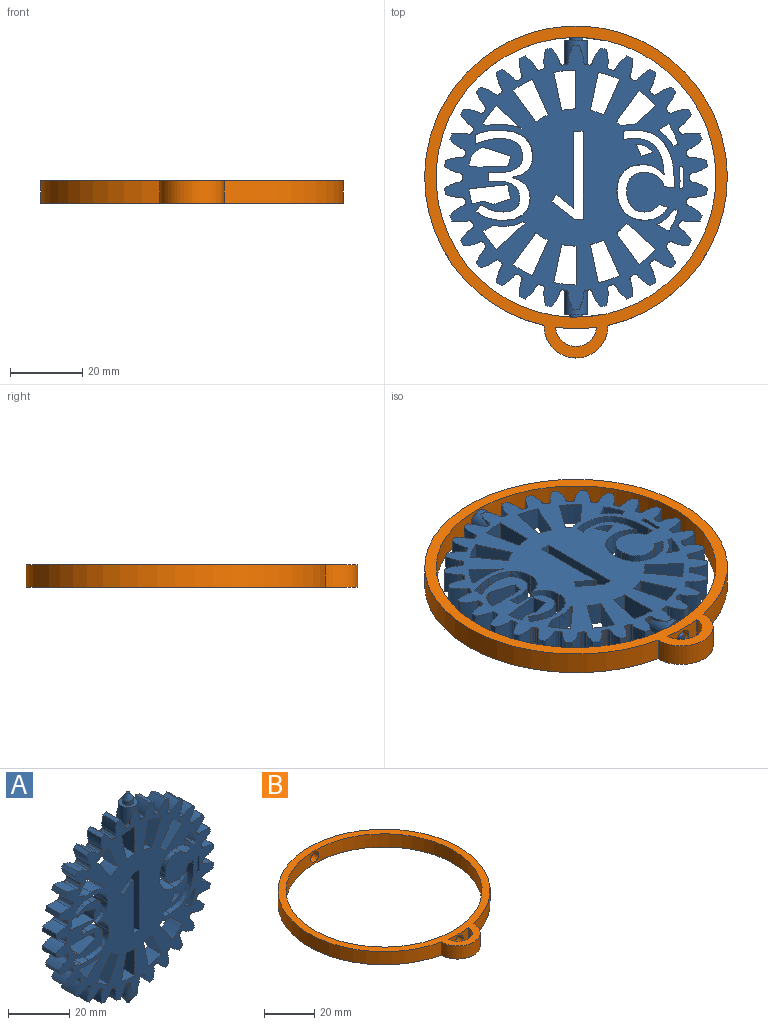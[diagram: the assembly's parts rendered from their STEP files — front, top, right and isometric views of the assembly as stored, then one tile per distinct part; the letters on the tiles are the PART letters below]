
ASSEMBLY  parts=2 mates=1
PART A: 350 faces, bbox 72.9x6.4x83.8 mm
  f0: cylinder r=36.58mm len=0.84mm, axis (0,1,0), area 0mm2, adj f24,f95,f341
  f1: cylinder r=36.58mm len=0.84mm, axis (0,1,0), area 0mm2, adj f24,f92,f341
  f2: cylinder r=36.58mm len=0.84mm, axis (0,1,0), area 0mm2, adj f3,f25,f341
  f3: extruded ~4.4x1.33mm, area 2.4mm2, adj f2,f4,f25,f341
  f4: cylinder r=0.84mm len=1.95mm, axis (0,1,0), area 1.8mm2, adj f3,f25,f91,f341
  f5: extruded ~4.4x1.33mm, area 2.4mm2, adj f6,f25,f47,f341
  f6: cylinder r=0.84mm len=1.95mm, axis (0,1,0), area 1.8mm2, adj f5,f25,f96,f341
  f7: cylinder r=36.58mm len=0.84mm, axis (0,1,0), area 0mm2, adj f12,f25,f336
  f8: cylinder r=36.58mm len=0.84mm, axis (0,1,0), area 0mm2, adj f18,f25,f336
  f9: cylinder r=36.58mm len=0.84mm, axis (0,1,0), area 0mm2, adj f17,f24,f336
  f10: cylinder r=36.58mm len=0.84mm, axis (0,1,0), area 0mm2, adj f11,f24,f336
  f11: extruded ~4.4x1.33mm, area 2.4mm2, adj f10,f14,f24,f336
  f12: extruded ~4.4x1.33mm, area 2.4mm2, adj f7,f15,f25,f336
  f13: cylinder r=31.43mm len=6.35mm, axis (0,1,0), area 4.6mm2, adj f14,f15,f24,f25,f196,f336
  f14: cylinder r=0.84mm len=1.95mm, axis (0,1,0), area 1.8mm2, adj f11,f13,f24,f336
  f15: cylinder r=0.84mm len=1.95mm, axis (0,1,0), area 1.8mm2, adj f12,f13,f25,f336
  f16: cylinder r=31.43mm len=6.35mm, axis (0,1,0), area 4.6mm2, adj f19,f20,f24,f25,f198,f336
  f17: extruded ~4.4x1.33mm, area 2.4mm2, adj f9,f19,f24,f336
  f18: extruded ~4.4x1.33mm, area 2.4mm2, adj f8,f20,f25,f336
  f19: cylinder r=0.84mm len=1.95mm, axis (0,1,0), area 1.8mm2, adj f16,f17,f24,f336
  f20: cylinder r=0.84mm len=1.95mm, axis (0,1,0), area 1.8mm2, adj f16,f18,f25,f336
  f21: plane 6.35x2.78mm, normal (0.1,0,-0.99), area 17.8mm2, adj f23,f24,f25,f333
  f22: plane 6.35x2.47mm, normal (-0.31,0,0.95), area 16.5mm2, adj f24,f25,f200,f327
  f23: extruded ~6.35x1.68mm, area 10.7mm2, adj f21,f24,f25,f199
  f24: plane 73.15x72.91mm, normal (0,-1,0), area 2651.2mm2, adj f0,f1,f9,f10,f11,f13,f14,f16
  f25: plane 73.15x72.91mm, normal (0,1,0), area 2651.2mm2, adj f2,f3,f4,f5,f6,f7,f8,f12
  f26: cylinder r=36.58mm len=6.35mm, axis (0,1,0), area 10.7mm2, adj f24,f25,f190,f195
  f27: cylinder r=36.58mm len=6.35mm, axis (0,1,0), area 10.7mm2, adj f24,f25,f185,f192
  f28: cylinder r=36.58mm len=6.35mm, axis (0,1,0), area 10.7mm2, adj f24,f25,f175,f187
  f29: cylinder r=36.58mm len=6.35mm, axis (0,1,0), area 10.7mm2, adj f24,f25,f170,f182
  f30: cylinder r=36.58mm len=6.35mm, axis (0,1,0), area 10.7mm2, adj f24,f25,f177,f180
  f31: cylinder r=36.58mm len=6.35mm, axis (0,1,0), area 10.7mm2, adj f24,f25,f165,f172
  f32: cylinder r=36.58mm len=6.35mm, axis (0,1,0), area 10.7mm2, adj f24,f25,f55,f167
  f33: cylinder r=36.58mm len=6.35mm, axis (0,1,0), area 10.7mm2, adj f24,f25,f150,f162
  f34: cylinder r=36.58mm len=6.35mm, axis (0,1,0), area 10.7mm2, adj f24,f25,f157,f160
  f35: cylinder r=36.58mm len=6.35mm, axis (0,1,0), area 10.7mm2, adj f24,f25,f145,f152
  f36: cylinder r=36.58mm len=6.35mm, axis (0,1,0), area 10.7mm2, adj f24,f25,f147,f197
  f37: cylinder r=36.58mm len=6.35mm, axis (0,1,0), area 10.7mm2, adj f24,f25,f142,f155
  f38: cylinder r=36.58mm len=6.35mm, axis (0,1,0), area 10.7mm2, adj f24,f25,f137,f140
  f39: cylinder r=36.58mm len=6.35mm, axis (0,1,0), area 10.7mm2, adj f24,f25,f132,f135
  f40: cylinder r=36.58mm len=6.35mm, axis (0,1,0), area 10.7mm2, adj f24,f25,f127,f130
  f41: cylinder r=36.58mm len=6.35mm, axis (0,1,0), area 10.7mm2, adj f24,f25,f110,f122
  f42: cylinder r=36.58mm len=6.35mm, axis (0,1,0), area 10.7mm2, adj f24,f25,f117,f120
  f43: cylinder r=36.58mm len=6.35mm, axis (0,1,0), area 10.7mm2, adj f24,f25,f105,f112
  f44: cylinder r=36.58mm len=6.35mm, axis (0,1,0), area 10.7mm2, adj f24,f25,f107,f125
  f45: cylinder r=36.58mm len=6.35mm, axis (0,1,0), area 10.7mm2, adj f24,f25,f102,f115
  f46: cylinder r=36.58mm len=6.35mm, axis (0,1,0), area 10.7mm2, adj f24,f25,f97,f100
  f47: cylinder r=36.58mm len=0.84mm, axis (0,1,0), area 0mm2, adj f5,f25,f341
  f48: cylinder r=36.58mm len=6.35mm, axis (0,1,0), area 10.7mm2, adj f24,f25,f87,f90
  f49: cylinder r=36.58mm len=6.35mm, axis (0,1,0), area 10.7mm2, adj f24,f25,f75,f82
  f50: cylinder r=36.58mm len=6.35mm, axis (0,1,0), area 10.7mm2, adj f24,f25,f65,f77
  f51: cylinder r=36.58mm len=6.35mm, axis (0,1,0), area 10.7mm2, adj f24,f25,f72,f85
  f52: cylinder r=36.58mm len=6.35mm, axis (0,1,0), area 10.7mm2, adj f24,f25,f67,f70
  f53: cylinder r=36.58mm len=6.35mm, axis (0,1,0), area 10.7mm2, adj f24,f25,f62,f80
  f54: cylinder r=36.58mm len=6.35mm, axis (0,1,0), area 10.7mm2, adj f24,f25,f57,f60
  f55: extruded ~6.35x4.24mm, area 29.4mm2, adj f24,f25,f32,f58
  f56: cylinder r=31.43mm len=6.35mm, axis (0,1,0), area 4.6mm2, adj f24,f25,f58,f59
  f57: extruded ~6.35x4.24mm, area 29.4mm2, adj f24,f25,f54,f59
  f58: cylinder r=0.84mm len=6.35mm, axis (0,1,0), area 8.1mm2, adj f24,f25,f55,f56
  f59: cylinder r=0.84mm len=6.35mm, axis (0,1,0), area 8.1mm2, adj f24,f25,f56,f57
  f60: extruded ~6.35x4.51mm, area 29.4mm2, adj f24,f25,f54,f63
  f61: cylinder r=31.43mm len=6.35mm, axis (0,1,0), area 4.6mm2, adj f24,f25,f63,f64
  f62: extruded ~6.35x3.77mm, area 29.4mm2, adj f24,f25,f53,f64
  f63: cylinder r=0.84mm len=6.35mm, axis (0,1,0), area 8.1mm2, adj f24,f25,f60,f61
  f64: cylinder r=0.84mm len=6.35mm, axis (0,1,0), area 8.1mm2, adj f24,f25,f61,f62
  f65: extruded ~6.35x4.16mm, area 29.4mm2, adj f24,f25,f50,f68
  f66: cylinder r=31.43mm len=6.35mm, axis (0,1,0), area 4.6mm2, adj f24,f25,f68,f69
  f67: extruded ~6.35x4.34mm, area 29.4mm2, adj f24,f25,f52,f69
  f68: cylinder r=0.84mm len=6.35mm, axis (0,1,0), area 8.1mm2, adj f24,f25,f65,f66
  f69: cylinder r=0.84mm len=6.35mm, axis (0,1,0), area 8.1mm2, adj f24,f25,f66,f67
  f70: extruded ~6.35x3.66mm, area 29.4mm2, adj f24,f25,f52,f73
  f71: cylinder r=31.43mm len=6.35mm, axis (0,1,0), area 4.6mm2, adj f24,f25,f73,f74
  f72: extruded ~6.35x4.56mm, area 29.4mm2, adj f24,f25,f51,f74
  f73: cylinder r=0.84mm len=6.35mm, axis (0,1,0), area 8.1mm2, adj f24,f25,f70,f71
  f74: cylinder r=0.84mm len=6.35mm, axis (0,1,0), area 8.1mm2, adj f24,f25,f71,f72
  f75: extruded ~6.35x4.47mm, area 29.4mm2, adj f24,f25,f49,f78
  f76: cylinder r=31.43mm len=6.35mm, axis (0,1,0), area 4.6mm2, adj f24,f25,f78,f79
  f77: extruded ~6.35x3.93mm, area 29.4mm2, adj f24,f25,f50,f79
  f78: cylinder r=0.84mm len=6.35mm, axis (0,1,0), area 8.1mm2, adj f24,f25,f75,f76
  f79: cylinder r=0.84mm len=6.35mm, axis (0,1,0), area 8.1mm2, adj f24,f25,f76,f77
  f80: extruded ~6.35x4.59mm, area 29.4mm2, adj f24,f25,f53,f83
  f81: cylinder r=31.43mm len=6.35mm, axis (0,1,0), area 4.6mm2, adj f24,f25,f83,f84
  f82: extruded ~6.35x3.35mm, area 29.4mm2, adj f24,f25,f49,f84
  f83: cylinder r=0.84mm len=6.35mm, axis (0,1,0), area 8.1mm2, adj f24,f25,f80,f81
  f84: cylinder r=0.84mm len=6.35mm, axis (0,1,0), area 8.1mm2, adj f24,f25,f81,f82
  f85: extruded ~6.35x3.48mm, area 29.4mm2, adj f24,f25,f51,f88
  f86: cylinder r=31.43mm len=6.35mm, axis (0,1,0), area 4.6mm2, adj f24,f25,f88,f89
  f87: extruded ~6.35x4.58mm, area 29.4mm2, adj f24,f25,f48,f89
  f88: cylinder r=0.84mm len=6.35mm, axis (0,1,0), area 8.1mm2, adj f24,f25,f85,f86
  f89: cylinder r=0.84mm len=6.35mm, axis (0,1,0), area 8.1mm2, adj f24,f25,f86,f87
  f90: extruded ~6.35x4.03mm, area 29.4mm2, adj f24,f25,f48,f93
  f91: cylinder r=31.43mm len=6.35mm, axis (0,1,0), area 4.3mm2, adj f4,f24,f25,f93,f94,f341
  f92: extruded ~4.4x1.33mm, area 2.4mm2, adj f1,f24,f94,f341
  f93: cylinder r=0.84mm len=6.35mm, axis (0,1,0), area 8.1mm2, adj f24,f25,f90,f91
  f94: cylinder r=0.84mm len=1.95mm, axis (0,1,0), area 1.8mm2, adj f24,f91,f92,f341
  f95: extruded ~4.4x1.33mm, area 2.4mm2, adj f0,f24,f98,f341
  f96: cylinder r=31.43mm len=6.35mm, axis (0,1,0), area 4.6mm2, adj f6,f24,f25,f98,f99,f341
  f97: extruded ~6.35x4.03mm, area 29.4mm2, adj f24,f25,f46,f99
  f98: cylinder r=0.84mm len=1.95mm, axis (0,1,0), area 1.8mm2, adj f24,f95,f96,f341
  f99: cylinder r=0.84mm len=6.35mm, axis (0,1,0), area 8.1mm2, adj f24,f25,f96,f97
  f100: extruded ~6.35x4.58mm, area 29.4mm2, adj f24,f25,f46,f103
  f101: cylinder r=31.43mm len=6.35mm, axis (0,1,0), area 4.6mm2, adj f24,f25,f103,f104
  f102: extruded ~6.35x3.48mm, area 29.4mm2, adj f24,f25,f45,f104
  f103: cylinder r=0.84mm len=6.35mm, axis (0,1,0), area 8.1mm2, adj f24,f25,f100,f101
  f104: cylinder r=0.84mm len=6.35mm, axis (0,1,0), area 8.1mm2, adj f24,f25,f101,f102
  f105: extruded ~6.35x3.35mm, area 29.4mm2, adj f24,f25,f43,f108
  f106: cylinder r=31.43mm len=6.35mm, axis (0,1,0), area 4.6mm2, adj f24,f25,f108,f109
  f107: extruded ~6.35x4.59mm, area 29.4mm2, adj f24,f25,f44,f109
  f108: cylinder r=0.84mm len=6.35mm, axis (0,1,0), area 8.1mm2, adj f24,f25,f105,f106
  f109: cylinder r=0.84mm len=6.35mm, axis (0,1,0), area 8.1mm2, adj f24,f25,f106,f107
  f110: extruded ~6.35x3.93mm, area 29.4mm2, adj f24,f25,f41,f113
  f111: cylinder r=31.43mm len=6.35mm, axis (0,1,0), area 4.6mm2, adj f24,f25,f113,f114
  f112: extruded ~6.35x4.47mm, area 29.4mm2, adj f24,f25,f43,f114
  f113: cylinder r=0.84mm len=6.35mm, axis (0,1,0), area 8.1mm2, adj f24,f25,f110,f111
  f114: cylinder r=0.84mm len=6.35mm, axis (0,1,0), area 8.1mm2, adj f24,f25,f111,f112
  f115: extruded ~6.35x4.56mm, area 29.4mm2, adj f24,f25,f45,f118
  f116: cylinder r=31.43mm len=6.35mm, axis (0,1,0), area 4.6mm2, adj f24,f25,f118,f119
  f117: extruded ~6.35x3.66mm, area 29.4mm2, adj f24,f25,f42,f119
  f118: cylinder r=0.84mm len=6.35mm, axis (0,1,0), area 8.1mm2, adj f24,f25,f115,f116
  f119: cylinder r=0.84mm len=6.35mm, axis (0,1,0), area 8.1mm2, adj f24,f25,f116,f117
  f120: extruded ~6.35x4.34mm, area 29.4mm2, adj f24,f25,f42,f123
  f121: cylinder r=31.43mm len=6.35mm, axis (0,1,0), area 4.6mm2, adj f24,f25,f123,f124
  f122: extruded ~6.35x4.16mm, area 29.4mm2, adj f24,f25,f41,f124
  f123: cylinder r=0.84mm len=6.35mm, axis (0,1,0), area 8.1mm2, adj f24,f25,f120,f121
  f124: cylinder r=0.84mm len=6.35mm, axis (0,1,0), area 8.1mm2, adj f24,f25,f121,f122
  f125: extruded ~6.35x3.77mm, area 29.4mm2, adj f24,f25,f44,f128
  f126: cylinder r=31.43mm len=6.35mm, axis (0,1,0), area 4.6mm2, adj f24,f25,f128,f129
  f127: extruded ~6.35x4.51mm, area 29.4mm2, adj f24,f25,f40,f129
  f128: cylinder r=0.84mm len=6.35mm, axis (0,1,0), area 8.1mm2, adj f24,f25,f125,f126
  f129: cylinder r=0.84mm len=6.35mm, axis (0,1,0), area 8.1mm2, adj f24,f25,f126,f127
  f130: extruded ~6.35x4.24mm, area 29.4mm2, adj f24,f25,f40,f133
  f131: cylinder r=31.43mm len=6.35mm, axis (0,1,0), area 4.6mm2, adj f24,f25,f133,f134
  f132: extruded ~6.35x4.24mm, area 29.4mm2, adj f24,f25,f39,f134
  f133: cylinder r=0.84mm len=6.35mm, axis (0,1,0), area 8.1mm2, adj f24,f25,f130,f131
  f134: cylinder r=0.84mm len=6.35mm, axis (0,1,0), area 8.1mm2, adj f24,f25,f131,f132
  f135: extruded ~6.35x4.51mm, area 29.4mm2, adj f24,f25,f39,f138
  f136: cylinder r=31.43mm len=6.35mm, axis (0,1,0), area 4.6mm2, adj f24,f25,f138,f139
  f137: extruded ~6.35x3.77mm, area 29.4mm2, adj f24,f25,f38,f139
  f138: cylinder r=0.84mm len=6.35mm, axis (0,1,0), area 8.1mm2, adj f24,f25,f135,f136
  f139: cylinder r=0.84mm len=6.35mm, axis (0,1,0), area 8.1mm2, adj f24,f25,f136,f137
  f140: extruded ~6.35x4.59mm, area 29.4mm2, adj f24,f25,f38,f143
  f141: cylinder r=31.43mm len=6.35mm, axis (0,1,0), area 4.6mm2, adj f24,f25,f143,f144
  f142: extruded ~6.35x3.35mm, area 29.4mm2, adj f24,f25,f37,f144
  f143: cylinder r=0.84mm len=6.35mm, axis (0,1,0), area 8.1mm2, adj f24,f25,f140,f141
  f144: cylinder r=0.84mm len=6.35mm, axis (0,1,0), area 8.1mm2, adj f24,f25,f141,f142
  f145: extruded ~6.35x3.48mm, area 29.4mm2, adj f24,f25,f35,f148
  f146: cylinder r=31.43mm len=6.35mm, axis (0,1,0), area 4.6mm2, adj f24,f25,f148,f149
  f147: extruded ~6.35x4.58mm, area 29.4mm2, adj f24,f25,f36,f149
  f148: cylinder r=0.84mm len=6.35mm, axis (0,1,0), area 8.1mm2, adj f24,f25,f145,f146
  f149: cylinder r=0.84mm len=6.35mm, axis (0,1,0), area 8.1mm2, adj f24,f25,f146,f147
  f150: extruded ~6.35x3.66mm, area 29.4mm2, adj f24,f25,f33,f153
  f151: cylinder r=31.43mm len=6.35mm, axis (0,1,0), area 4.6mm2, adj f24,f25,f153,f154
  f152: extruded ~6.35x4.56mm, area 29.4mm2, adj f24,f25,f35,f154
  f153: cylinder r=0.84mm len=6.35mm, axis (0,1,0), area 8.1mm2, adj f24,f25,f150,f151
  f154: cylinder r=0.84mm len=6.35mm, axis (0,1,0), area 8.1mm2, adj f24,f25,f151,f152
  f155: extruded ~6.35x4.47mm, area 29.4mm2, adj f24,f25,f37,f158
  f156: cylinder r=31.43mm len=6.35mm, axis (0,1,0), area 4.6mm2, adj f24,f25,f158,f159
  f157: extruded ~6.35x3.93mm, area 29.4mm2, adj f24,f25,f34,f159
  f158: cylinder r=0.84mm len=6.35mm, axis (0,1,0), area 8.1mm2, adj f24,f25,f155,f156
  f159: cylinder r=0.84mm len=6.35mm, axis (0,1,0), area 8.1mm2, adj f24,f25,f156,f157
  f160: extruded ~6.35x4.16mm, area 29.4mm2, adj f24,f25,f34,f163
  f161: cylinder r=31.43mm len=6.35mm, axis (0,1,0), area 4.6mm2, adj f24,f25,f163,f164
  f162: extruded ~6.35x4.34mm, area 29.4mm2, adj f24,f25,f33,f164
  f163: cylinder r=0.84mm len=6.35mm, axis (0,1,0), area 8.1mm2, adj f24,f25,f160,f161
  f164: cylinder r=0.84mm len=6.35mm, axis (0,1,0), area 8.1mm2, adj f24,f25,f161,f162
  f165: extruded ~6.35x3.77mm, area 29.4mm2, adj f24,f25,f31,f168
  f166: cylinder r=31.43mm len=6.35mm, axis (0,1,0), area 4.6mm2, adj f24,f25,f168,f169
  f167: extruded ~6.35x4.51mm, area 29.4mm2, adj f24,f25,f32,f169
  f168: cylinder r=0.84mm len=6.35mm, axis (0,1,0), area 8.1mm2, adj f24,f25,f165,f166
  f169: cylinder r=0.84mm len=6.35mm, axis (0,1,0), area 8.1mm2, adj f24,f25,f166,f167
  f170: extruded ~6.35x3.35mm, area 29.4mm2, adj f24,f25,f29,f173
  f171: cylinder r=31.43mm len=6.35mm, axis (0,1,0), area 4.6mm2, adj f24,f25,f173,f174
  f172: extruded ~6.35x4.59mm, area 29.4mm2, adj f24,f25,f31,f174
  f173: cylinder r=0.84mm len=6.35mm, axis (0,1,0), area 8.1mm2, adj f24,f25,f170,f171
  f174: cylinder r=0.84mm len=6.35mm, axis (0,1,0), area 8.1mm2, adj f24,f25,f171,f172
  f175: extruded ~6.35x4.34mm, area 29.4mm2, adj f24,f25,f28,f178
  f176: cylinder r=31.43mm len=6.35mm, axis (0,1,0), area 4.6mm2, adj f24,f25,f178,f179
  f177: extruded ~6.35x4.16mm, area 29.4mm2, adj f24,f25,f30,f179
  f178: cylinder r=0.84mm len=6.35mm, axis (0,1,0), area 8.1mm2, adj f24,f25,f175,f176
  f179: cylinder r=0.84mm len=6.35mm, axis (0,1,0), area 8.1mm2, adj f24,f25,f176,f177
  f180: extruded ~6.35x3.93mm, area 29.4mm2, adj f24,f25,f30,f183
  f181: cylinder r=31.43mm len=6.35mm, axis (0,1,0), area 4.6mm2, adj f24,f25,f183,f184
  f182: extruded ~6.35x4.47mm, area 29.4mm2, adj f24,f25,f29,f184
  f183: cylinder r=0.84mm len=6.35mm, axis (0,1,0), area 8.1mm2, adj f24,f25,f180,f181
  f184: cylinder r=0.84mm len=6.35mm, axis (0,1,0), area 8.1mm2, adj f24,f25,f181,f182
  f185: extruded ~6.35x4.56mm, area 29.4mm2, adj f24,f25,f27,f188
  f186: cylinder r=31.43mm len=6.35mm, axis (0,1,0), area 4.6mm2, adj f24,f25,f188,f189
  f187: extruded ~6.35x3.66mm, area 29.4mm2, adj f24,f25,f28,f189
  f188: cylinder r=0.84mm len=6.35mm, axis (0,1,0), area 8.1mm2, adj f24,f25,f185,f186
  f189: cylinder r=0.84mm len=6.35mm, axis (0,1,0), area 8.1mm2, adj f24,f25,f186,f187
  f190: extruded ~6.35x4.58mm, area 29.4mm2, adj f24,f25,f26,f193
  f191: cylinder r=31.43mm len=6.35mm, axis (0,1,0), area 4.6mm2, adj f24,f25,f193,f194
  f192: extruded ~6.35x3.48mm, area 29.4mm2, adj f24,f25,f27,f194
  f193: cylinder r=0.84mm len=6.35mm, axis (0,1,0), area 8.1mm2, adj f24,f25,f190,f191
  f194: cylinder r=0.84mm len=6.35mm, axis (0,1,0), area 8.1mm2, adj f24,f25,f191,f192
  f195: extruded ~6.35x4.03mm, area 29.4mm2, adj f24,f25,f26,f196
  f196: cylinder r=0.84mm len=6.35mm, axis (0,1,0), area 8.1mm2, adj f13,f24,f25,f195
  f197: extruded ~6.35x4.03mm, area 29.4mm2, adj f24,f25,f36,f198
  f198: cylinder r=0.84mm len=6.35mm, axis (0,1,0), area 8.1mm2, adj f16,f24,f25,f197
  f199: extruded ~14.34x11.09mm, area 131.5mm2, adj f23,f24,f25,f213
  f200: extruded ~6.35x2.35mm, area 20.5mm2, adj f22,f24,f25,f201
  f201: extruded ~6.35x4.35mm, area 29.3mm2, adj f24,f25,f200,f202
  f202: extruded ~6.35x5.6mm, area 39.4mm2, adj f24,f25,f201,f203
  f203: extruded ~6.35x6.01mm, area 41.5mm2, adj f24,f25,f202,f204
  f204: extruded ~6.35x5.41mm, area 37.4mm2, adj f24,f25,f203,f205
  f205: extruded ~6.35x5.14mm, area 35.9mm2, adj f24,f25,f204,f206
  f206: extruded ~6.35x3.42mm, area 22.4mm2, adj f24,f25,f205,f207
  f207: extruded ~6.35x2.44mm, area 20.7mm2, adj f24,f25,f206,f208
  f208: plane 6.35x0.2mm, normal (0,0,1), area 1.3mm2, adj f24,f25,f207,f209
  f209: extruded ~7.61x6.35mm, area 51.2mm2, adj f24,f25,f208,f210
  f210: extruded ~6.35x6.06mm, area 43mm2, adj f24,f25,f209,f211
  f211: extruded ~6.35x3.04mm, area 19.6mm2, adj f24,f25,f210,f212
  f212: plane 6.35x2.39mm, normal (1,0,0), area 15.2mm2, adj f24,f25,f211,f213
  f213: extruded ~6.35x3.07mm, area 19.7mm2, adj f24,f25,f199,f212
  f214: plane 6.35x2.7mm, normal (0,0,1), area 17.2mm2, adj f24,f25,f215,f222
  f215: plane 24.42x6.35mm, normal (-1,0,0), area 155.1mm2, adj f24,f25,f214,f216
  f216: plane 6.35x2.34mm, normal (0,0,-1), area 14.8mm2, adj f24,f25,f215,f217
  f217: plane 6.46x6.35mm, normal (0.61,0,-0.79), area 51.9mm2, adj f24,f25,f216,f218
  f218: plane 6.35x1.9mm, normal (0.79,0,0.61), area 15.3mm2, adj f24,f25,f217,f219
  f219: extruded ~6.35x3.97mm, area 32.6mm2, adj f24,f25,f218,f220
  f220: extruded ~6.35x0.78mm, area 6.8mm2, adj f24,f25,f219,f221
  f221: extruded ~6.35x4.11mm, area 26.1mm2, adj f24,f25,f220,f222
  f222: plane 17.4x6.35mm, normal (1,0,0), area 110.5mm2, adj f24,f25,f214,f221
  f223: extruded ~6.35x3.83mm, area 26.3mm2, adj f24,f25,f224,f250
  f224: extruded ~6.35x4.47mm, area 32.1mm2, adj f24,f25,f223,f225
  f225: extruded ~6.35x5.53mm, area 37.3mm2, adj f24,f25,f224,f226
  f226: extruded ~6.35x4.14mm, area 26.7mm2, adj f24,f25,f225,f227
  f227: extruded ~6.35x3.46mm, area 25.1mm2, adj f24,f25,f226,f228
  f228: plane 6.35x1.87mm, normal (0.8,0,0.6), area 14.8mm2, adj f24,f25,f227,f229
  f229: extruded ~6.35x3.24mm, area 23mm2, adj f24,f25,f228,f230
  f230: extruded ~6.35x3.02mm, area 19.5mm2, adj f24,f25,f229,f231
  f231: extruded ~6.35x3.33mm, area 22.6mm2, adj f24,f25,f230,f232
  f232: extruded ~6.35x2.81mm, area 20.1mm2, adj f24,f25,f231,f233
  f233: extruded ~6.35x3.5mm, area 25.6mm2, adj f24,f25,f232,f234
  f234: extruded ~6.35x4.52mm, area 30.4mm2, adj f24,f25,f233,f235
  f235: plane 6.35x2.44mm, normal (0,0,-1), area 15.5mm2, adj f24,f25,f234,f236
  f236: plane 6.35x2.38mm, normal (1,0,0), area 15.1mm2, adj f24,f25,f235,f237
  f237: plane 6.35x2.41mm, normal (0,0,1), area 15.3mm2, adj f24,f25,f236,f238
  f238: extruded ~6.98x6.35mm, area 59.5mm2, adj f24,f25,f237,f239
  f239: extruded ~6.35x6.33mm, area 58.3mm2, adj f24,f25,f238,f240
  f240: extruded ~6.35x3.4mm, area 21.8mm2, adj f24,f25,f239,f241
  f241: extruded ~6.35x3.38mm, area 22.8mm2, adj f24,f25,f240,f242
  f242: plane 6.35x2.64mm, normal (1,0,0), area 16.8mm2, adj f24,f25,f241,f243
  f243: extruded ~6.35x3.13mm, area 21mm2, adj f24,f25,f242,f244
  f244: extruded ~6.35x3.55mm, area 22.7mm2, adj f24,f25,f243,f245
  f245: extruded ~6.88x6.35mm, area 46.1mm2, adj f24,f25,f244,f246
  f246: extruded ~6.35x5.37mm, area 38.8mm2, adj f24,f25,f245,f247
  f247: extruded ~6.35x3.94mm, area 27.3mm2, adj f24,f25,f246,f248
  f248: extruded ~6.35x4.36mm, area 30.7mm2, adj f24,f25,f247,f249
  f249: plane 6.35x0.13mm, normal (-1,0,0), area 0.8mm2, adj f24,f25,f248,f250
  f250: extruded ~6.35x3.72mm, area 27.2mm2, adj f24,f25,f223,f249
  f251: cylinder r=19.05mm len=6.35mm, axis (0,-1,0), area 25.3mm2, adj f24,f25,f252,f254
  f252: plane 8.02x7.22mm, normal (-0.67,0,0.74), area 68.5mm2, adj f24,f25,f251,f253
  f253: cylinder r=29.84mm len=6.35mm, axis (0,-1,0), area 39.7mm2, adj f24,f25,f252,f254
  f254: plane 8.73x6.35mm, normal (0.81,0,-0.59), area 68.5mm2, adj f24,f25,f251,f253
  f255: cylinder r=19.05mm len=6.35mm, axis (0,-1,0), area 23.4mm2, adj f24,f25,f256,f258
  f256: extruded ~6.35x4.37mm, area 31.2mm2, adj f24,f25,f255,f257
  f257: extruded ~6.35x0.44mm, area 3.5mm2, adj f24,f25,f256,f258
  f258: plane 6.35x3.22mm, normal (-0.31,0,-0.95), area 21.5mm2, adj f24,f25,f255,f257
  f259: extruded ~6.35x4.41mm, area 38.9mm2, adj f24,f25,f260,f262
  f260: plane 6.35x3.04mm, normal (0.5,0,0.87), area 22.3mm2, adj f24,f25,f259,f261
  f261: cylinder r=29.84mm len=6.35mm, axis (0,-1,0), area 39.7mm2, adj f24,f25,f260,f262
  f262: plane 6.35x1.45mm, normal (-0.31,0,-0.95), area 9.7mm2, adj f24,f25,f259,f261
  f263: extruded ~6.35x4.19mm, area 26.7mm2, adj f24,f25,f264,f267
  f264: plane 6.35x1.05mm, normal (0.1,0,0.99), area 6.7mm2, adj f24,f25,f263,f265
  f265: cylinder r=29.84mm len=6.35mm, axis (0,-1,0), area 39.7mm2, adj f24,f25,f264,f266
  f266: plane 6.35x0.86mm, normal (0.1,0,-0.99), area 5.5mm2, adj f24,f25,f265,f267
  f267: extruded ~6.35x1.85mm, area 11.8mm2, adj f24,f25,f263,f266
  f268: cylinder r=19.05mm len=6.35mm, axis (0,-1,0), area 25.3mm2, adj f24,f25,f269,f271
  f269: plane 10.56x6.35mm, normal (0.98,0,0.21), area 68.5mm2, adj f24,f25,f268,f270
  f270: cylinder r=29.84mm len=6.35mm, axis (0,-1,0), area 39.7mm2, adj f24,f25,f269,f271
  f271: plane 9.86x6.35mm, normal (-0.91,0,-0.41), area 68.5mm2, adj f24,f25,f268,f270
  f272: cylinder r=19.05mm len=6.35mm, axis (0,-1,0), area 25.3mm2, adj f24,f25,f273,f276
  f273: plane 6.35x4.97mm, normal (-0.31,0,-0.95), area 33.2mm2, adj f24,f25,f272,f274
  f274: extruded ~6.35x0.69mm, area 4.8mm2, adj f24,f25,f273,f349
  f275: cylinder r=29.84mm len=6.35mm, axis (0,-1,0), area 24.8mm2, adj f24,f25,f276,f348
  f276: plane 10.73x6.35mm, normal (0.1,0,0.99), area 68.5mm2, adj f24,f25,f272,f275
  f277: plane 6.35x2.23mm, normal (0.1,0,-0.99), area 14.2mm2, adj f24,f25,f278,f346
  f278: cylinder r=29.84mm len=6.35mm, axis (0,-1,0), area 6.5mm2, adj f24,f25,f277,f347
  f279: extruded ~6.35x0.68mm, area 4.6mm2, adj f24,f25,f280,f347
  f280: plane 7.68x6.35mm, normal (-0.31,0,0.95), area 51.3mm2, adj f24,f25,f279,f281
  f281: cylinder r=19.05mm len=6.35mm, axis (0,-1,0), area 16.9mm2, adj f24,f25,f280,f282
  f282: extruded ~6.35x3.06mm, area 19.6mm2, adj f24,f25,f281,f283
  f283: plane 6.35x3.99mm, normal (0,0,-1), area 25.4mm2, adj f24,f25,f282,f346
  f284: cylinder r=19.05mm len=6.35mm, axis (0,-1,0), area 11.2mm2, adj f24,f25,f285,f290
  f285: plane 8.73x6.35mm, normal (0.81,0,0.59), area 68.5mm2, adj f24,f25,f284,f286
  f286: cylinder r=29.84mm len=6.35mm, axis (0,-1,0), area 39.7mm2, adj f24,f25,f285,f287
  f287: plane 6.35x5.81mm, normal (-0.67,0,-0.74), area 49.6mm2, adj f24,f25,f286,f288
  f288: extruded ~6.35x0.15mm, area 1mm2, adj f24,f25,f287,f289
  f289: extruded ~6.35x3.53mm, area 22.6mm2, adj f24,f25,f288,f290
  f290: extruded ~6.35x0.12mm, area 0.8mm2, adj f24,f25,f284,f289
  f291: cylinder r=19.05mm len=6.35mm, axis (0,-1,0), area 25.3mm2, adj f24,f25,f292,f294
  f292: plane 9.86x6.35mm, normal (-0.91,0,0.41), area 68.5mm2, adj f24,f25,f291,f293
  f293: cylinder r=29.84mm len=6.35mm, axis (0,-1,0), area 39.7mm2, adj f24,f25,f292,f294
  f294: plane 10.56x6.35mm, normal (0.98,0,-0.21), area 68.5mm2, adj f24,f25,f291,f293
  f295: cylinder r=19.05mm len=6.35mm, axis (0,-1,0), area 25.3mm2, adj f24,f25,f296,f298
  f296: plane 10.79x6.35mm, normal (-1,0,0), area 68.5mm2, adj f24,f25,f295,f297
  f297: cylinder r=29.84mm len=6.35mm, axis (0,-1,0), area 39.7mm2, adj f24,f25,f296,f298
  f298: plane 10.56x6.35mm, normal (0.98,0,0.21), area 68.5mm2, adj f24,f25,f295,f297
  f299: cylinder r=19.05mm len=6.35mm, axis (0,-1,0), area 4.5mm2, adj f24,f25,f300,f304
  f300: plane 8.02x7.22mm, normal (-0.67,0,-0.74), area 68.5mm2, adj f24,f25,f299,f301
  f301: cylinder r=29.84mm len=6.35mm, axis (0,-1,0), area 39.7mm2, adj f24,f25,f300,f302
  f302: plane 6.35x2.85mm, normal (0.5,0,0.87), area 20.9mm2, adj f24,f25,f301,f303
  f303: extruded ~6.35x2.77mm, area 17.7mm2, adj f24,f25,f302,f304
  f304: extruded ~6.35x5.6mm, area 37mm2, adj f24,f25,f299,f303
  f305: cylinder r=19.05mm len=6.35mm, axis (0,-1,0), area 25.3mm2, adj f24,f25,f306,f308
  f306: plane 9.86x6.35mm, normal (-0.91,0,-0.41), area 68.5mm2, adj f24,f25,f305,f307
  f307: cylinder r=29.84mm len=6.35mm, axis (0,-1,0), area 39.7mm2, adj f24,f25,f306,f308
  f308: plane 8.73x6.35mm, normal (0.81,0,0.59), area 68.5mm2, adj f24,f25,f305,f307
  f309: cylinder r=19.05mm len=6.35mm, axis (0,-1,0), area 25.3mm2, adj f24,f25,f310,f312
  f310: plane 10.56x6.35mm, normal (0.98,0,-0.21), area 68.5mm2, adj f24,f25,f309,f311
  f311: cylinder r=29.84mm len=6.35mm, axis (0,-1,0), area 39.7mm2, adj f24,f25,f310,f312
  f312: plane 10.79x6.35mm, normal (-1,0,0), area 68.5mm2, adj f24,f25,f309,f311
  f313: cylinder r=19.05mm len=6.35mm, axis (0,-1,0), area 25.3mm2, adj f24,f25,f314,f316
  f314: plane 8.73x6.35mm, normal (0.81,0,-0.59), area 68.5mm2, adj f24,f25,f313,f315
  f315: cylinder r=29.84mm len=6.35mm, axis (0,-1,0), area 39.7mm2, adj f24,f25,f314,f316
  f316: plane 9.86x6.35mm, normal (-0.91,0,0.41), area 68.5mm2, adj f24,f25,f313,f315
  f317: extruded ~6.35x3.74mm, area 23.8mm2, adj f24,f25,f318,f321
  f318: plane 6.35x0.83mm, normal (0.5,0,-0.87), area 6.1mm2, adj f24,f25,f317,f319
  f319: cylinder r=29.84mm len=6.35mm, axis (0,-1,0), area 39.7mm2, adj f24,f25,f318,f320
  f320: plane 7.18x6.47mm, normal (-0.67,0,0.74), area 61.4mm2, adj f24,f25,f319,f321
  f321: extruded ~6.35x6.28mm, area 41mm2, adj f24,f25,f317,f320
  f322: extruded ~6.35x3.16mm, area 27.1mm2, adj f24,f25,f323,f326
  f323: plane 6.35x1.22mm, normal (-0.31,0,0.95), area 8.1mm2, adj f24,f25,f322,f324
  f324: cylinder r=29.84mm len=6.35mm, axis (0,-1,0), area 39.7mm2, adj f24,f25,f323,f325
  f325: plane 6.35x3.4mm, normal (0.5,0,-0.87), area 24.9mm2, adj f24,f25,f324,f326
  f326: extruded ~6.35x1.89mm, area 13.6mm2, adj f24,f25,f322,f325
  f327: extruded ~6.35x1.25mm, area 11.1mm2, adj f22,f24,f25,f334
  f328: extruded ~6.35x4.28mm, area 29mm2, adj f24,f25,f329,f335
  f329: extruded ~6.35x3.78mm, area 25.8mm2, adj f24,f25,f328,f330
  f330: extruded ~6.35x3.66mm, area 25.6mm2, adj f24,f25,f329,f331
  f331: extruded ~6.35x2.8mm, area 18.4mm2, adj f24,f25,f330,f332
  f332: extruded ~6.35x2.01mm, area 16.9mm2, adj f24,f25,f331,f333
  f333: extruded ~6.35x1.66mm, area 11.5mm2, adj f21,f24,f25,f332
  f334: extruded ~6.35x2.81mm, area 19mm2, adj f24,f25,f327,f335
  f335: extruded ~6.35x3.69mm, area 26.3mm2, adj f24,f25,f328,f334
  f336: cylinder r=3.17mm len=6.8mm, axis (0,0,-1), area 95.1mm2, adj f7,f8,f9,f10,f11,f12,f13,f14
  f337: plane 6.35x6.35mm, normal (0,0,1), area 20.3mm2, adj f336,f338
  f338: cylinder r=1.91mm len=3.81mm, axis (0,0,-1), area 19.3mm2, adj f337,f340
  f339: plane 1.27x1.27mm, normal (0,0,1), area 1.3mm2, adj f340
  f340: cone r=0.64mm half-angle=30deg, axis (0,0,-1), area 20.3mm2, adj f338,f339
  f341: cylinder r=3.17mm len=6.83mm, axis (0,0,1), area 95.1mm2, adj f0,f1,f2,f3,f4,f5,f6,f47
  f342: plane 6.35x6.35mm, normal (0,0,-1), area 20.3mm2, adj f341,f343
  f343: cylinder r=1.91mm len=3.81mm, axis (0,0,1), area 19.3mm2, adj f342,f345
  f344: plane 1.27x1.27mm, normal (0,0,-1), area 1.3mm2, adj f345
  f345: cone r=1.91mm half-angle=30deg, axis (0,0,1), area 20.3mm2, adj f343,f344
  f346: cylinder r=5.08mm len=6.35mm, axis (0,-1,0), area 10.4mm2, adj f24,f25,f277,f283
  f347: cylinder r=5.08mm len=6.35mm, axis (0,-1,0), area 33.5mm2, adj f24,f25,f278,f279
  f348: cylinder r=0.51mm len=6.35mm, axis (0,-1,0), area 5.9mm2, adj f24,f25,f275,f349
  f349: cylinder r=5.08mm len=6.35mm, axis (0,-1,0), area 29.7mm2, adj f24,f25,f274,f348
PART B: 9 faces, bbox 84.1x92.2x6.4 mm
  f0: cylinder r=42.04mm len=11.42mm, axis (0,0,-1), area 56.3mm2, adj f3,f4,f5,f7
  f1: cylinder r=42.04mm len=84.07mm, axis (0,0,-1), area 1546.9mm2, adj f3,f4,f6,f8
  f2: cylinder r=38.86mm len=77.72mm, axis (0,0,-1), area 1517.6mm2, adj f3,f4,f5,f6
  f3: plane 92.21x84.07mm, normal (0,0,1), area 879.1mm2, adj f0,f1,f2,f7,f8
  f4: plane 92.21x84.07mm, normal (0,0,-1), area 879.1mm2, adj f0,f1,f2,f7,f8
  f5: cylinder r=2.29mm len=4.57mm, axis (0,-1,0), area 45.6mm2, adj f0,f2
  f6: cylinder r=2.29mm len=4.57mm, axis (0,-1,0), area 45.6mm2, adj f1,f2
  f7: cylinder r=5.72mm len=11.42mm, axis (0,0,1), area 109.4mm2, adj f0,f3,f4
  f8: cylinder r=8.9mm len=17.79mm, axis (0,0,1), area 179.9mm2, adj f1,f3,f4
PLACE A rot(axis=(1,0,0),90deg) t=(-23.68,-21.43,-9.6)mm
PLACE B rot(axis=(1,0,0),0deg) t=(-23.68,-21.39,-15.95)mm fixed
MATE revolute B.f5 <-> A.f336  axis (0,-1,0) through (-23.68,-60.16,-12.78)mm
